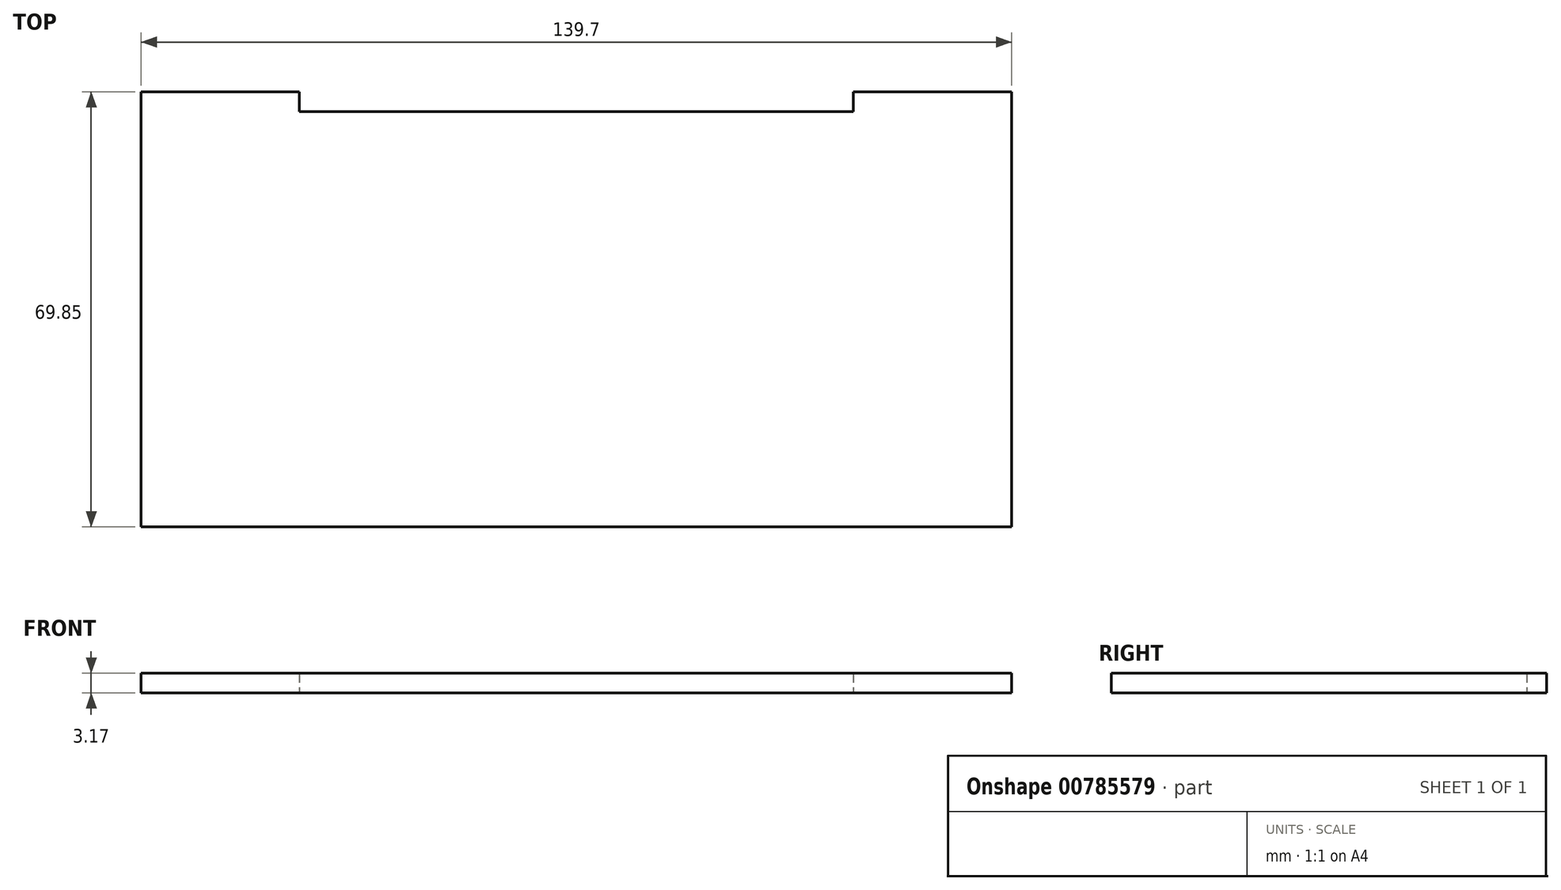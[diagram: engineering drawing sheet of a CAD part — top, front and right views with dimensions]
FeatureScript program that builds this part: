
annotation { "Feature Type Name" : "Feature", "Feature Type Description" : "" }
export const myFeature = defineFeature(function(context is Context, id is Id, definition is map)
    precondition{}
    {
        {
            var Q0;
            Q0=qCreatedBy(makeId("Top.planeOp"),FACE);
            var sketch = newSketch(context, id + "F0", { "sketchPlane" : qUnion([Q0])});
            skLineSegment(sketch, "E0.bottom", {"start": v(69.85, 33.34) * mm, "end": v(-69.85, 33.34) * mm});
            skLineSegment(sketch, "E0.top", {"start": v(69.85, -33.34) * mm, "end": v(-69.85, -33.34) * mm});
            skLineSegment(sketch, "E0.left", {"start": v(69.85, 33.34) * mm, "end": v(69.85, -33.34) * mm});
            skLineSegment(sketch, "E0.right", {"start": v(-69.85, 33.34) * mm, "end": v(-69.85, -33.34) * mm});
            skPoint(sketch, "E0.middle", {"position": v(0, 0) * mm});
            skLineSegment(sketch, "E1.bottom", {"start": v(-69.85, 33.34) * mm, "end": v(69.85, 33.34) * mm});
            skLineSegment(sketch, "E1.top", {"start": v(-69.85, 36.51) * mm, "end": v(69.85, 36.51) * mm});
            skLineSegment(sketch, "E1.left", {"start": v(-69.85, 33.34) * mm, "end": v(-69.85, 36.51) * mm});
            skLineSegment(sketch, "E1.right", {"start": v(69.85, 33.34) * mm, "end": v(69.85, 36.51) * mm});
            skLineSegment(sketch, "E2.bottom", {"start": v(-69.85, 33.34) * mm, "end": v(-44.45, 33.34) * mm});
            skLineSegment(sketch, "E2.top", {"start": v(-69.85, 36.51) * mm, "end": v(-44.45, 36.51) * mm});
            skLineSegment(sketch, "E2.right", {"start": v(-44.45, 33.34) * mm, "end": v(-44.45, 36.51) * mm});
            skLineSegment(sketch, "E3.bottom", {"start": v(69.85, 33.34) * mm, "end": v(44.45, 33.34) * mm});
            skLineSegment(sketch, "E3.top", {"start": v(69.85, 36.51) * mm, "end": v(44.45, 36.51) * mm});
            skLineSegment(sketch, "E3.right", {"start": v(44.45, 33.34) * mm, "end": v(44.45, 36.51) * mm});
            skSolve(sketch);
        }
        {
            var Q0;
            Q0=makeQuery(id+"F0.imprint","IMPRINT",FACE,{"disambiguationData":[TD([[makeQuery(id+"F0.imprint","IMPRINT",EDGE,{"derivedFrom":sQuery(id+"F0.wireOp",EDGE,"E0.top")}),-1.0]])]});
            var Q1;
            {var subQ0=sQuery(id+"F0.wireOp",EDGE,"E1.left");Q1=makeQuery(id+"F0.imprint","IMPRINT",FACE,{"disambiguationData":[TD([[makeQuery(id+"F0.imprint","IMPRINT",EDGE,{"derivedFrom":subQ0}),-1.0]])]});}
            var Q2;
            {var subQ2=sQuery(id+"F0.wireOp",EDGE,"E1.right");Q2=makeQuery(id+"F0.imprint","IMPRINT",FACE,{"disambiguationData":[TD([[makeQuery(id+"F0.imprint","IMPRINT",EDGE,{"derivedFrom":subQ2}),1.0]])]});}
            extrude(context, id + "F1", {"entities" : qUnion([Q0, Q1, Q2]), "depth" : 3.17 * mm, "offsetDistance" : 25.4 * mm});
        }
    });
